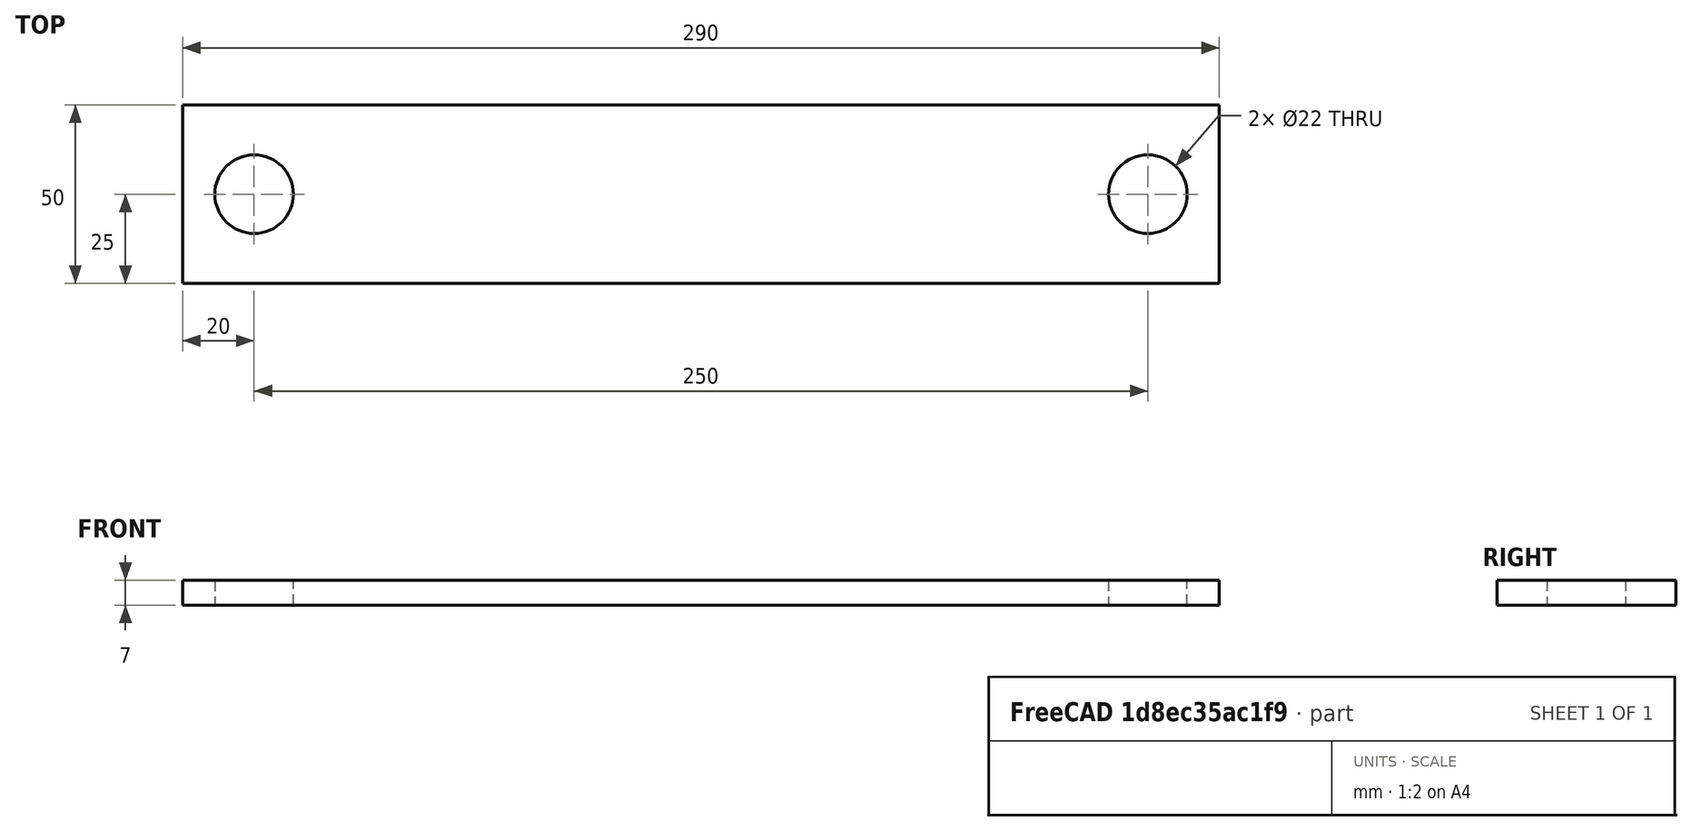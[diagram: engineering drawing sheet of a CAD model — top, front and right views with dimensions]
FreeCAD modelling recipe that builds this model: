
FCSTD DOCUMENT  (FreeCAD 0.19R24276 (Git))
Label: richag_300
License: All rights reserved
LicenseURL: http://en.wikipedia.org/wiki/All_rights_reserved
objects: Sketcher::SketchObject×1, PartDesign::Pad×1, PartDesign::Body×1
note: 4 computed .brp shape members not serialized (recipe doc carries the construction recipe); baked Part::Feature solids carry a one-line shape summary decoded from their .brp

FEATURE [Sketcher::SketchObject] Sketch
  FullyConstrained = false
  MapMode = 5
  Support = -> [XY_Plane]
  sketch-geometry (6):
    g0: Circle CenterX=2e-16 CenterY=0 CenterZ=0 NormalX=0 NormalY=0 NormalZ=1 AngleXU=0 Radius=11
    g1: Circle CenterX=250 CenterY=0 CenterZ=0 NormalX=0 NormalY=0 NormalZ=1 AngleXU=0 Radius=11
    g2: LineSegment StartX=-20 StartY=25 StartZ=0 EndX=270 EndY=25 EndZ=0
    g3: LineSegment StartX=270 StartY=25 StartZ=0 EndX=270 EndY=-25 EndZ=0
    g4: LineSegment StartX=270 StartY=-25 StartZ=0 EndX=-20 EndY=-25 EndZ=0
    g5: LineSegment StartX=-20 StartY=-25 StartZ=0 EndX=-20 EndY=25 EndZ=0
  constraints (16):
    c: Coincident(g2,g3)
    c: Coincident(g3,g4)
    c: Coincident(g4,g5)
    c: Coincident(g5,g2)
    c: Horizontal(g2)
    c: Horizontal(g4)
    c: Vertical(g3)
    c: Vertical(g5)
    c: Diameter(g0) = 22
    c: Diameter(g1) = 22
    c: DistanceX(g0,g1) = 250
    c: DistanceX(g4,g0) = 20
    c: Coincident(g0,g-1)
    c: DistanceX(g1,g3) = 20
    c: DistanceY(g0,g2) = 25
    c: DistanceY(g4,g0) = 25
FEATURE [PartDesign::Pad] Pad
  Direction = (1,1,1)
  Length = 7
  Length2 = 100
  Profile = -> Sketch
  Type = 0
FEATURE [PartDesign::Body] Body
  Group = -> [Sketch,Pad]
  Origin = -> Origin
  Tip = -> Pad
